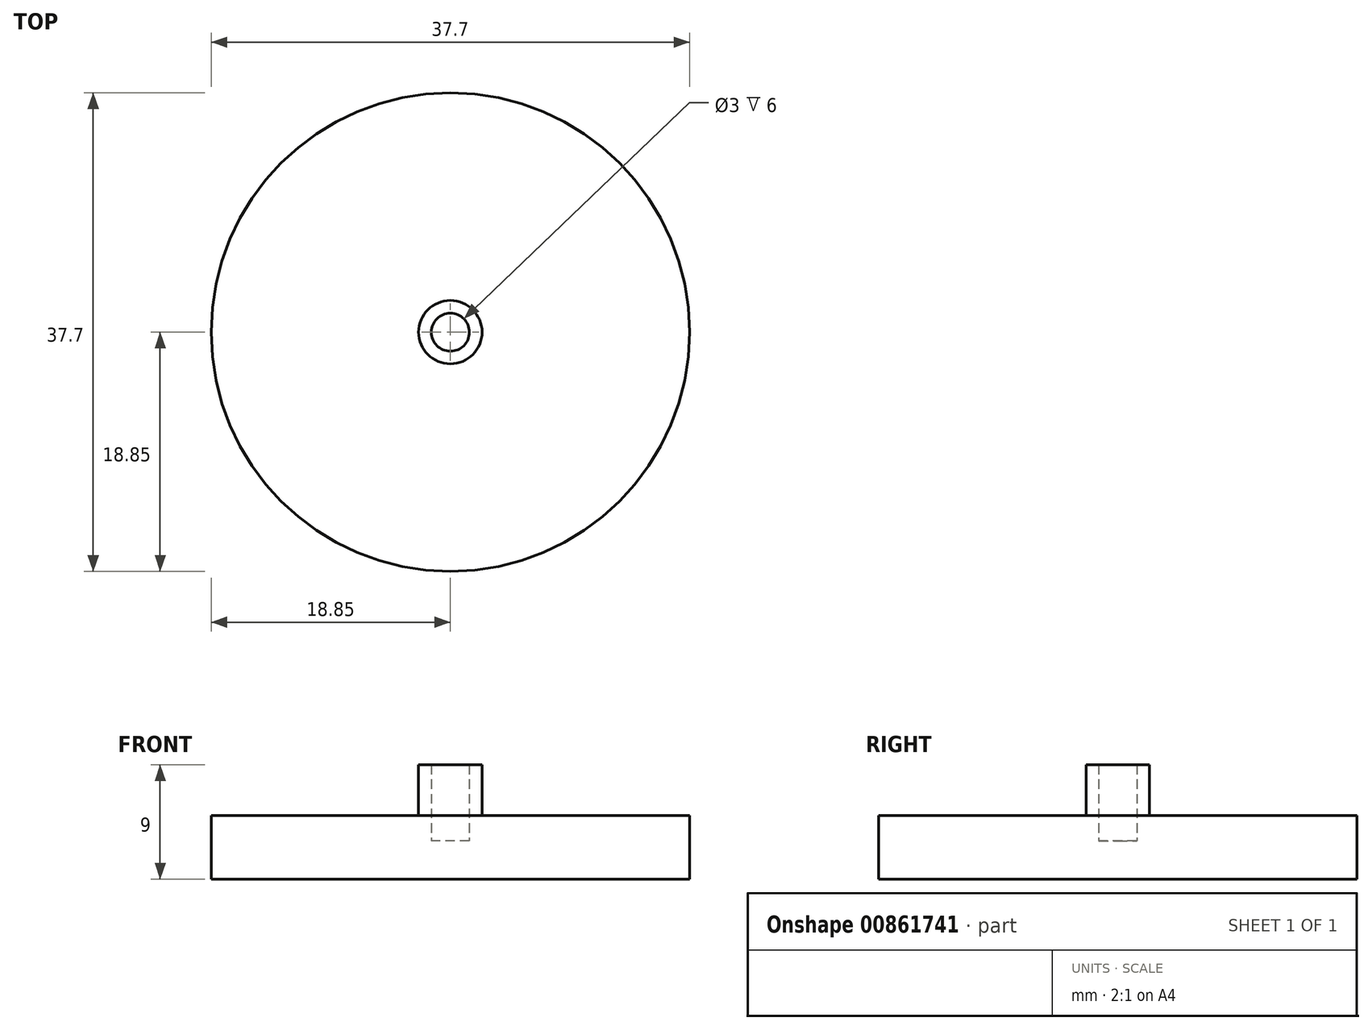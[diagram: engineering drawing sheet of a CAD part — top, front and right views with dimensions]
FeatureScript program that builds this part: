
annotation { "Feature Type Name" : "Feature", "Feature Type Description" : "" }
export const myFeature = defineFeature(function(context is Context, id is Id, definition is map)
    precondition{}
    {
        {
            var Q0;
            Q0=qCreatedBy(makeId("Top.planeOp"),FACE);
            var sketch = newSketch(context, id + "F0", { "sketchPlane" : qUnion([Q0])});
            skCircle(sketch, "E0", {"center": v(0, 0) * mm, "radius": 18.85 * mm});
            skCircle(sketch, "E1", {"center": v(0, 0) * mm, "radius": 1.5 * mm});
            skCircle(sketch, "E2", {"center": v(0, 0) * mm, "radius": 2.5 * mm});
            skSolve(sketch);
        }
        {
            var Q0;
            Q0=makeQuery(id+"F0.imprint","IMPRINT",FACE,{"disambiguationData":[TD([[makeQuery(id+"F0.imprint","IMPRINT",EDGE,{"derivedFrom":sQuery(id+"F0.wireOp",EDGE,"E0")}),1.0]])]});
            var Q1;
            Q1=makeQuery(id+"F0.imprint","IMPRINT",FACE,{"disambiguationData":[TD([[makeQuery(id+"F0.imprint","IMPRINT",EDGE,{"derivedFrom":sQuery(id+"F0.wireOp",EDGE,"E1")}),-1.0]])]});
            extrude(context, id + "F1", {"entities" : qUnion([Q0, Q1]), "depth" : 5 * mm, "offsetDistance" : 25 * mm});
        }
        {
            var Q0;
            Q0=makeQuery(id+"F0.imprint","IMPRINT",FACE,{"disambiguationData":[TD([[makeQuery(id+"F0.imprint","IMPRINT",EDGE,{"derivedFrom":sQuery(id+"F0.wireOp",EDGE,"E1")}),-1.0]])]});
            var Q1;
            Q1=sQuery(id+"F0.wireOp",EDGE,"E1");
            var Q2;
            Q2=sQuery(id+"F0.wireOp",EDGE,"E2");
            extrude(context, id + "F2", {"entities" : qUnion([Q0]), "operationType" : NewBodyOperationType.ADD, "surfaceEntities" : qUnion([Q1, Q2]), "depth" : 9 * mm, "offsetDistance" : 25 * mm});
        }
        {
            var Q0;
            Q0 = qSketchRegion(id + "F0", true);
            var Q1;
            Q1=makeQuery(id+"F0.imprint","IMPRINT",FACE,{"disambiguationData":[TD([[makeQuery(id+"F0.imprint","IMPRINT",EDGE,{"derivedFrom":sQuery(id+"F0.wireOp",EDGE,"E1")}),1.0]])]});
            extrude(context, id + "F3", {"entities" : qUnion([Q0, Q1]), "operationType" : NewBodyOperationType.ADD, "depth" : 3 * mm, "offsetDistance" : 25 * mm});
        }
    });
